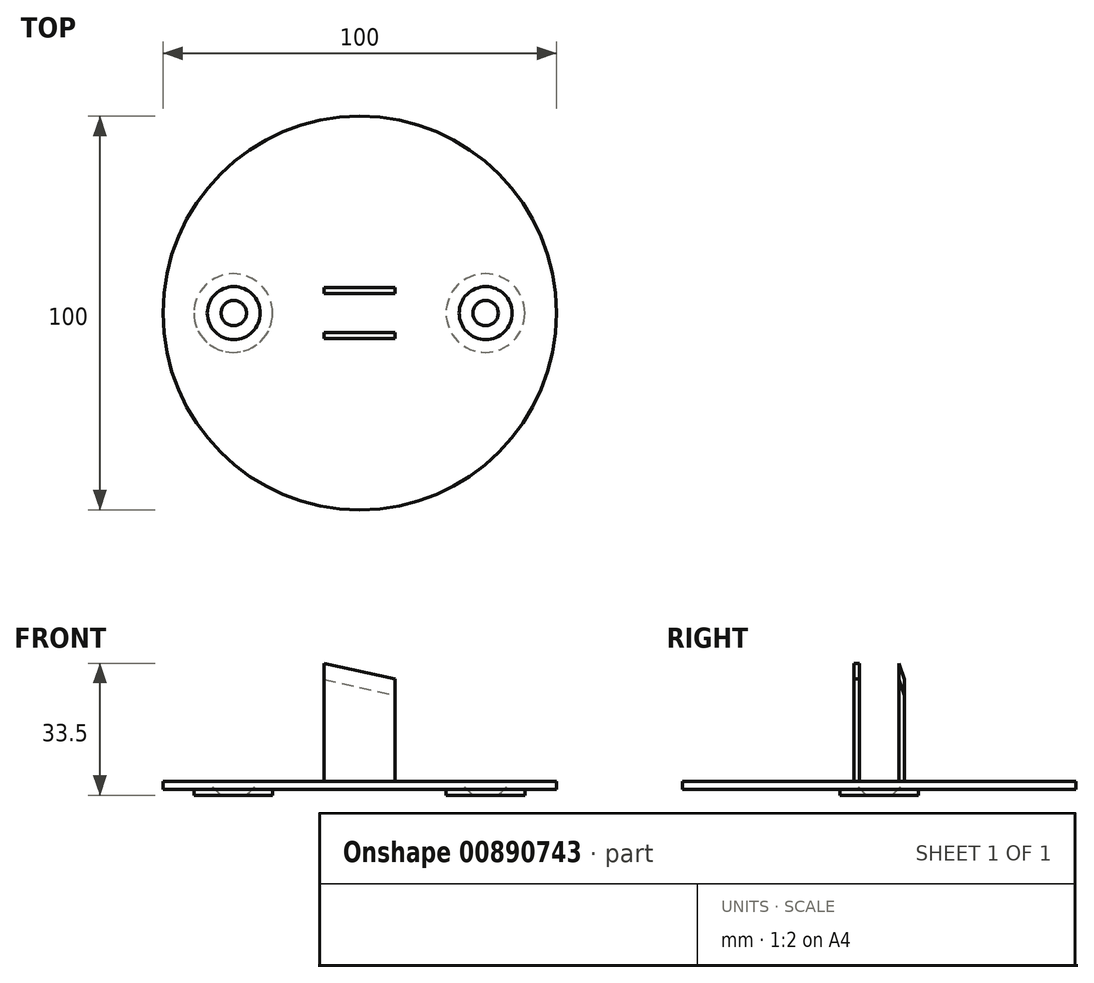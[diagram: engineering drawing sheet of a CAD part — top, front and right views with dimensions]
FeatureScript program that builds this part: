
annotation { "Feature Type Name" : "Feature", "Feature Type Description" : "" }
export const myFeature = defineFeature(function(context is Context, id is Id, definition is map)
    precondition{}
    {
        {
            var Q0;
            Q0=qCreatedBy(makeId("Top.planeOp"),FACE);
            var sketch = newSketch(context, id + "F0", { "sketchPlane" : qUnion([Q0])});
            skCircle(sketch, "E0", {"center": v(0, 0) * mm, "radius": 50 * mm});
            skSolve(sketch);
        }
        {
            var Q0;
            Q0=qSketchRegion(id+"F0",true);
            extrude(context, id + "F1", {"entities" : qUnion([Q0]), "depth" : 2 * mm, "offsetDistance" : 25 * mm});
        }
        {
            var Q0;
            Q0=makeQuery(id+"F1.opExtrude","CAP_FACE",FACE,{"disambiguationData":[OSD([sQuery(id+"F0.wireOp",EDGE,"E0")])],"isStart":false});
            var sketch = newSketch(context, id + "F2", { "sketchPlane" : qUnion([Q0])});
            skLineSegment(sketch, "E1", {"start": v(-50, 0) * mm, "end": v(50, 0) * mm, "construction": true});
            skPoint(sketch, "E2", {"position": v(-32, 0) * mm});
            skPoint(sketch, "E3", {"position": v(32, 0) * mm});
            skSolve(sketch);
        }
        {
            var Q0;
            Q0=makeQuery(id+"F1.opExtrude","CAP_FACE",FACE,{"disambiguationData":[OSD([sQuery(id+"F0.wireOp",EDGE,"E0")])],"isStart":true});
            var sketch = newSketch(context, id + "F3", { "sketchPlane" : qUnion([Q0])});
            skCircle(sketch, "E4", {"center": v(31.94, 0) * mm, "radius": 10 * mm});
            skCircle(sketch, "E5", {"center": v(-32.13, 0) * mm, "radius": 10 * mm});
            skSolve(sketch);
        }
        {
            var Q0;
            Q0=qSketchRegion(id+"F3",true);
            extrude(context, id + "F4", {"entities" : qUnion([Q0]), "operationType" : NewBodyOperationType.ADD, "depth" : 1.5 * mm, "offsetDistance" : 25 * mm});
        }
        {
            var Q0;
            Q0=sQuery(id+"F2.wireOp",VERTEX,"E2");
            var Q1;
            Q1=sQuery(id+"F2.wireOp",VERTEX,"E3");
            var Q2;
            Q2=makeQuery(id+"F1.opExtrude","SWEPT_BODY",BODY,{"disambiguationData":[OSD([sQuery(id+"F0.wireOp",EDGE,"E0")])]});
            hole(context, id + "F5", {"style" : HoleStyle.C_SINK, "endStyle" : HoleEndStyle.THROUGH, "standardTappedOrClearance" : lookupTablePath({ "fit" : "Close", "standard" : "ISO", "size" : "M6", "type" : "Clearance" }), "standardBlindInLast" : lookupTablePath({ "fit" : "Close", "standard" : "ISO", "size" : "M6", "type" : "Clearance" }), "holeDiameter" : 6.4 * mm, "cSinkDiameter" : 13.44 * mm, "cSinkAngle" : 90 * degree, "majorDiameter" : 5 * mm, "isTappedThrough" : true, "tappedDepth" : 12 * mm, "tapClearance" : 3, "locations" : qUnion([Q0, Q1]), "scope" : qUnion([Q2])});
        }
        {
            var Q0;
            Q0=makeQuery(id+"F1.opExtrude","CAP_FACE",FACE,{"disambiguationData":[OSD([sQuery(id+"F0.wireOp",EDGE,"E0")])],"isStart":false});
            var sketch = newSketch(context, id + "F6", { "sketchPlane" : qUnion([Q0])});
            skLineSegment(sketch, "E6.bottom", {"start": v(-9, 6.45) * mm, "end": v(9, 6.45) * mm});
            skLineSegment(sketch, "E6.top", {"start": v(-9, 5) * mm, "end": v(9, 5) * mm});
            skLineSegment(sketch, "E6.left", {"start": v(-9, 6.45) * mm, "end": v(-9, 5) * mm});
            skLineSegment(sketch, "E6.right", {"start": v(9, 6.45) * mm, "end": v(9, 5) * mm});
            skLineSegment(sketch, "E7.bottom", {"start": v(-9, -5) * mm, "end": v(9, -5) * mm});
            skLineSegment(sketch, "E7.top", {"start": v(-9, -6.45) * mm, "end": v(9, -6.45) * mm});
            skLineSegment(sketch, "E7.left", {"start": v(-9, -5) * mm, "end": v(-9, -6.45) * mm});
            skLineSegment(sketch, "E7.right", {"start": v(9, -5) * mm, "end": v(9, -6.45) * mm});
            skSolve(sketch);
        }
        {
            var Q0;
            Q0=qSketchRegion(id+"F6",true);
            extrude(context, id + "F7", {"entities" : qUnion([Q0]), "operationType" : NewBodyOperationType.ADD, "depth" : 30 * mm, "offsetDistance" : 25 * mm});
        }
        {
            var Q0;
            Q0=makeQuery(id+"F7.opExtrude","SWEPT_FACE",FACE,{"disambiguationData":[OSD([sQuery(id+"F6.wireOp",EDGE,"E7.top")])]});
            var sketch = newSketch(context, id + "F8", { "sketchPlane" : qUnion([Q0])});
            skLineSegment(sketch, "E8", {"start": v(-9, 32) * mm, "end": v(9, 28) * mm});
            skLineSegment(sketch, "E9", {"start": v(9, 28) * mm, "end": v(9, 32) * mm});
            skLineSegment(sketch, "E10", {"start": v(9, 32) * mm, "end": v(-9, 32) * mm});
            skSolve(sketch);
        }
        {
            var Q0;
            Q0=qSketchRegion(id+"F8",true);
            extrude(context, id + "F9", {"entities" : qUnion([Q0]), "operationType" : NewBodyOperationType.REMOVE, "oppositeDirection" : true, "depth" : 25 * mm, "offsetDistance" : 25 * mm});
        }
        {
            var Q0;
            Q0=makeQuery(id+"F9.boolean.opBoolean","INTERSECT",EDGE,{"derivedFrom":[makeQuery(id+"F7.opExtrude","SWEPT_FACE",FACE,{"disambiguationData":[OSD([sQuery(id+"F6.wireOp",EDGE,"E6.bottom")])]}),makeQuery(id+"F9.opExtrude","SWEPT_FACE",FACE,{"disambiguationData":[OSD([sQuery(id+"F8.wireOp",EDGE,"E8")])]})]});
            var Q1;
            Q1=makeQuery(id+"F9.boolean.opBoolean","COPY",EDGE,{"derivedFrom":makeQuery(id+"F9.opExtrude","CAP_EDGE",EDGE,{"disambiguationData":[OSD([sQuery(id+"F8.wireOp",EDGE,"E8")])],"isStart":true})});
            chamfer(context, id + "F10", {"entities" : qUnion([Q0, Q1]), "chamferType" : ChamferType.OFFSET_ANGLE, "width" : 4 * mm, "oppositeDirection" : true, "angle" : 20 * degree, "tangentPropagation" : true});
        }
    });
